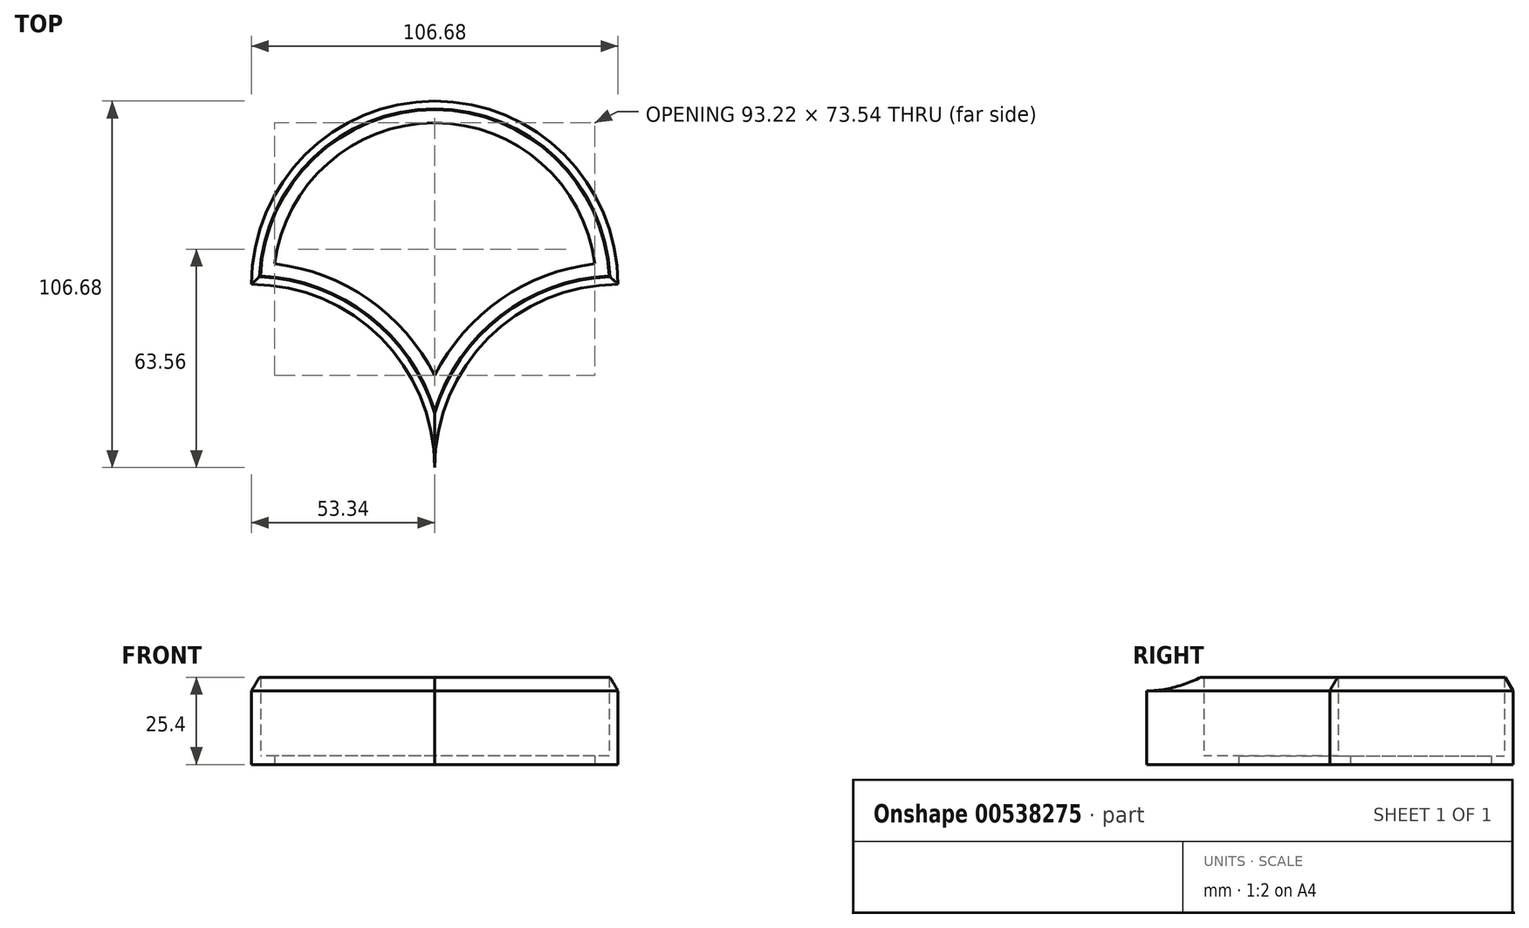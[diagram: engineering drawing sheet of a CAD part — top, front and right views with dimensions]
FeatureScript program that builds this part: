
annotation { "Feature Type Name" : "Feature", "Feature Type Description" : "" }
export const myFeature = defineFeature(function(context is Context, id is Id, definition is map)
    precondition{}
    {
        {
            var Q0;
            Q0=qCreatedBy(makeId("Top.planeOp"),FACE);
            var sketch = newSketch(context, id + "F0", { "sketchPlane" : qUnion([Q0])});
            skCircle(sketch, "E0", {"center": v(0, 0) * mm, "radius": 53.34 * mm});
            skPoint(sketch, "E1", {"position": v(0, -53.34) * mm});
            skPoint(sketch, "E2", {"position": v(-53.34, 0) * mm});
            skCircle(sketch, "E3", {"center": v(-53.34, -53.34) * mm, "radius": 53.34 * mm});
            skPoint(sketch, "E3.third.point", {"position": v(-87.32, -94.45) * mm});
            skLineSegment(sketch, "E4", {"start": v(-53.34, 0) * mm, "end": v(53.34, 0) * mm, "construction": true});
            skCircle(sketch, "E5", {"center": v(53.34, -53.34) * mm, "radius": 53.34 * mm});
            skPoint(sketch, "E5.third.point", {"position": v(77.9, -100.69) * mm});
            skSolve(sketch);
        }
        {
            var Q0;
            {var subQ0=sQuery(id+"F0.wireOp",EDGE,"E3");var subQ1=sQuery(id+"F0.wireOp",EDGE,"E0");var subQ2=makeQuery(id+"F0.imprint","INTERSECT",VERTEX,{"derivedFrom":[subQ1,subQ0]});Q0=makeQuery(id+"F0.imprint","IMPRINT",FACE,{"disambiguationData":[TD([[makeQuery(id+"F0.imprint","IMPRINT",EDGE,{"disambiguationData":[TD([[subQ2,1.0]])],"derivedFrom":subQ1}),1.0]])]});}
            extrude(context, id + "F1", {"entities" : qUnion([Q0]), "depth" : 25.4 * mm, "offsetDistance" : 25.4 * mm});
        }
        {
            var Q0;
            Q0=makeQuery(id+"F1.opExtrude","CAP_FACE",FACE,{"disambiguationData":[OSD([sQuery(id+"F0.wireOp",EDGE,"E0"),sQuery(id+"F0.wireOp",EDGE,"E3"),sQuery(id+"F0.wireOp",EDGE,"E5")])],"isStart":false});
            shell(context, id + "F2", {"entities" : qUnion([Q0]), "thickness" : 2.54 * mm});
        }
        {
            var Q0;
            Q0=makeQuery(id+"F1.opExtrude","CAP_EDGE",EDGE,{"disambiguationData":[OSD([sQuery(id+"F0.wireOp",EDGE,"E0")])],"isStart":false});
            var Q1;
            Q1=makeQuery(id+"F1.opExtrude","CAP_EDGE",EDGE,{"disambiguationData":[OSD([sQuery(id+"F0.wireOp",EDGE,"E3")])],"isStart":false});
            var Q2;
            Q2=makeQuery(id+"F1.opExtrude","CAP_EDGE",EDGE,{"disambiguationData":[OSD([sQuery(id+"F0.wireOp",EDGE,"E5")])],"isStart":false});
            chamfer(context, id + "F3", {"entities" : qUnion([Q0, Q1, Q2]), "chamferType" : ChamferType.OFFSET_ANGLE, "width" : 2.3 * mm, "oppositeDirection" : false, "angle" : 60 * degree, "tangentPropagation" : true});
        }
        {
            var Q0;
            Q0=makeQuery(id+"F1.opExtrude","CAP_FACE",FACE,{"disambiguationData":[OSD([sQuery(id+"F0.wireOp",EDGE,"E0"),sQuery(id+"F0.wireOp",EDGE,"E3"),sQuery(id+"F0.wireOp",EDGE,"E5")])],"isStart":true});
            var sketch = newSketch(context, id + "F4", { "sketchPlane" : qUnion([Q0])});
            skArc(sketch, "E6.0", {"start": v(46.6, -5.97) * mm, "mid": v(19.19, 4.39) * mm, "end": v(0, 26.55) * mm});
            skArc(sketch, "E6.1", {"start": v(-46.6, -5.97) * mm, "mid": v(0, -46.99) * mm, "end": v(46.6, -5.97) * mm});
            skArc(sketch, "E6.2", {"start": v(0, 26.55) * mm, "mid": v(-19.19, 4.39) * mm, "end": v(-46.6, -5.97) * mm});
            skSolve(sketch);
        }
        {
            var Q0;
            Q0=qSketchRegion(id+"F4",true);
            var Q1;
            Q1=makeQuery(id+"F1.opExtrude","SWEPT_BODY",BODY,{"disambiguationData":[OSD([sQuery(id+"F0.wireOp",EDGE,"E0"),sQuery(id+"F0.wireOp",EDGE,"E3"),sQuery(id+"F0.wireOp",EDGE,"E5")])]});
            extrude(context, id + "F5", {"entities" : qUnion([Q0]), "operationType" : NewBodyOperationType.REMOVE, "endBound" : BoundingType.UP_TO_BODY, "oppositeDirection" : true, "depth" : 25.4 * mm, "endBoundEntityBody" : qUnion([Q1]), "offsetDistance" : 25.4 * mm});
        }
    });
